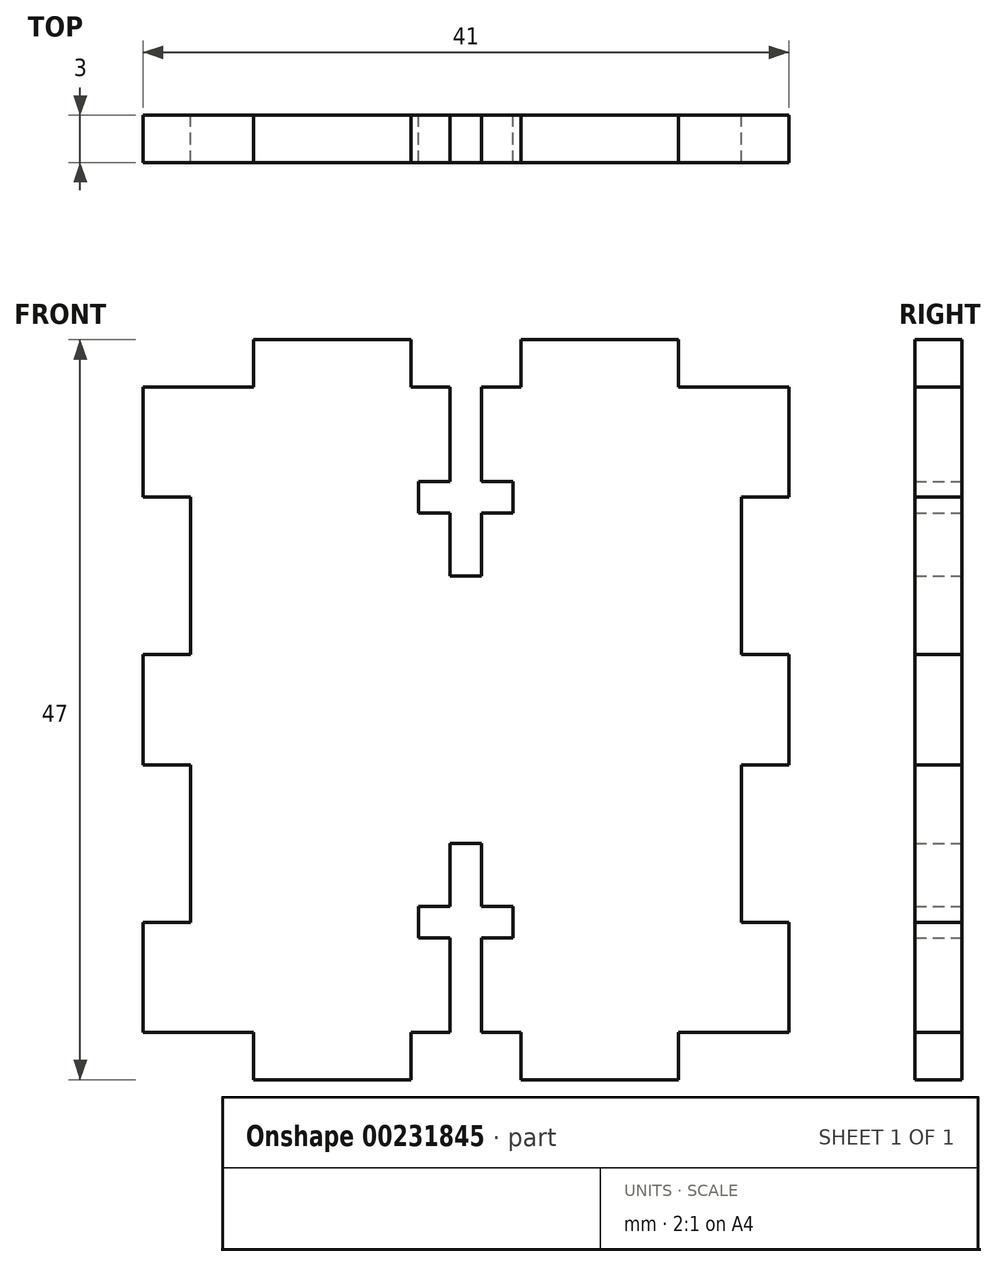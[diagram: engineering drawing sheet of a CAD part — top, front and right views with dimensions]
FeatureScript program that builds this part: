
annotation { "Feature Type Name" : "Feature", "Feature Type Description" : "" }
export const myFeature = defineFeature(function(context is Context, id is Id, definition is map)
    precondition{}
    {
        {
            var Q0;
            Q0=qCreatedBy(makeId("Front.planeOp"),FACE);
            var sketch = newSketch(context, id + "F0", { "sketchPlane" : qUnion([Q0])});
            skLineSegment(sketch, "E0", {"start": v(0, 0) * mm, "end": v(0, 3.5) * mm});
            skLineSegment(sketch, "E1", {"start": v(0, 3.5) * mm, "end": v(3, 3.5) * mm});
            skLineSegment(sketch, "E2", {"start": v(3, 3.5) * mm, "end": v(3, 13.5) * mm});
            skLineSegment(sketch, "E3", {"start": v(3, 13.5) * mm, "end": v(0, 13.5) * mm});
            skLineSegment(sketch, "E4", {"start": v(0, 13.5) * mm, "end": v(0, 20.5) * mm});
            skLineSegment(sketch, "E5", {"start": v(0, 20.5) * mm, "end": v(7, 20.5) * mm});
            skLineSegment(sketch, "E6", {"start": v(7, 20.5) * mm, "end": v(7, 23.5) * mm});
            skLineSegment(sketch, "E7", {"start": v(7, 23.5) * mm, "end": v(17, 23.5) * mm});
            skLineSegment(sketch, "E8", {"start": v(17, 23.5) * mm, "end": v(17, 20.5) * mm});
            skLineSegment(sketch, "E9", {"start": v(17, 20.5) * mm, "end": v(19.5, 20.5) * mm});
            skLineSegment(sketch, "E10", {"start": v(24, 20.5) * mm, "end": v(24, 23.5) * mm});
            skLineSegment(sketch, "E11.top", {"start": v(19.5, 8.5) * mm, "end": v(21.5, 8.5) * mm});
            skLineSegment(sketch, "E11.left", {"start": v(19.5, 20.5) * mm, "end": v(19.5, 14.5) * mm});
            skLineSegment(sketch, "E11.right", {"start": v(21.5, 20.5) * mm, "end": v(21.5, 14.5) * mm});
            skLineSegment(sketch, "E12.bottom", {"start": v(17.5, 14.5) * mm, "end": v(19.5, 14.5) * mm});
            skLineSegment(sketch, "E12.top", {"start": v(17.5, 12.5) * mm, "end": v(19.5, 12.5) * mm});
            skLineSegment(sketch, "E12.left", {"start": v(17.5, 14.5) * mm, "end": v(17.5, 12.5) * mm});
            skLineSegment(sketch, "E12.right", {"start": v(23.5, 14.5) * mm, "end": v(23.5, 12.5) * mm});
            skLineSegment(sketch, "E13.trimOffspring", {"start": v(21.5, 20.5) * mm, "end": v(24, 20.5) * mm});
            skLineSegment(sketch, "E14.trimOffspring", {"start": v(19.5, 12.5) * mm, "end": v(19.5, 8.5) * mm});
            skLineSegment(sketch, "E15.trimOffspring", {"start": v(21.5, 12.5) * mm, "end": v(21.5, 8.5) * mm});
            skPoint(sketch, "E16.trimOffspring.end.orphan", {"position": v(20.5, 0) * mm});
            skLineSegment(sketch, "E17", {"start": v(24, 23.5) * mm, "end": v(34, 23.5) * mm});
            skLineSegment(sketch, "E18", {"start": v(34, 23.5) * mm, "end": v(34, 20.5) * mm});
            skLineSegment(sketch, "E19", {"start": v(34, 20.5) * mm, "end": v(41, 20.5) * mm});
            skLineSegment(sketch, "E20", {"start": v(41, 20.5) * mm, "end": v(41, 13.5) * mm});
            skLineSegment(sketch, "E21", {"start": v(38, 13.5) * mm, "end": v(41, 13.5) * mm});
            skLineSegment(sketch, "E22", {"start": v(38, 13.5) * mm, "end": v(38, 3.5) * mm});
            skLineSegment(sketch, "E23", {"start": v(38, 3.5) * mm, "end": v(41, 3.5) * mm});
            skLineSegment(sketch, "E24", {"start": v(41, 3.5) * mm, "end": v(41, 0) * mm});
            skLineSegment(sketch, "E25", {"start": v(0, 0) * mm, "end": v(41, 0) * mm, "construction": true});
            skLineSegment(sketch, "E26.MirrorCS", {"start": v(17.5, -12.5) * mm, "end": v(19.5, -12.5) * mm});
            skLineSegment(sketch, "E27.MirrorCS", {"start": v(34, -20.5) * mm, "end": v(41, -20.5) * mm});
            skLineSegment(sketch, "E28.MirrorCS", {"start": v(38, -3.5) * mm, "end": v(41, -3.5) * mm});
            skLineSegment(sketch, "E29.MirrorCS", {"start": v(38, -13.5) * mm, "end": v(41, -13.5) * mm});
            skLineSegment(sketch, "E30.MirrorCS", {"start": v(21.5, -12.5) * mm, "end": v(21.5, -8.5) * mm});
            skLineSegment(sketch, "E31.MirrorCS", {"start": v(38, -13.5) * mm, "end": v(38, -3.5) * mm});
            skLineSegment(sketch, "E32.MirrorCS", {"start": v(34, -23.5) * mm, "end": v(34, -20.5) * mm});
            skLineSegment(sketch, "E33.MirrorCS", {"start": v(41, -20.5) * mm, "end": v(41, -13.5) * mm});
            skLineSegment(sketch, "E34.MirrorCS", {"start": v(19.5, -8.5) * mm, "end": v(21.5, -8.5) * mm});
            skLineSegment(sketch, "E35.MirrorCS", {"start": v(24, -23.5) * mm, "end": v(34, -23.5) * mm});
            skLineSegment(sketch, "E36.MirrorCS", {"start": v(21.5, -20.5) * mm, "end": v(24, -20.5) * mm});
            skLineSegment(sketch, "E37.MirrorCS", {"start": v(17.5, -14.5) * mm, "end": v(17.5, -12.5) * mm});
            skLineSegment(sketch, "E38.MirrorCS", {"start": v(19.5, -20.5) * mm, "end": v(19.5, -14.5) * mm});
            skLineSegment(sketch, "E39.MirrorCS", {"start": v(19.5, -12.5) * mm, "end": v(19.5, -8.5) * mm});
            skLineSegment(sketch, "E40.MirrorCS", {"start": v(17, -23.5) * mm, "end": v(17, -20.5) * mm});
            skLineSegment(sketch, "E41.MirrorCS", {"start": v(0, -20.5) * mm, "end": v(7, -20.5) * mm});
            skLineSegment(sketch, "E42.MirrorCS", {"start": v(17.5, -14.5) * mm, "end": v(19.5, -14.5) * mm});
            skLineSegment(sketch, "E43.MirrorCS", {"start": v(41, -3.5) * mm, "end": v(41, 0) * mm});
            skLineSegment(sketch, "E44.MirrorCS", {"start": v(0, -13.5) * mm, "end": v(0, -20.5) * mm});
            skLineSegment(sketch, "E45.MirrorCS", {"start": v(7, -23.5) * mm, "end": v(17, -23.5) * mm});
            skLineSegment(sketch, "E46.MirrorCS", {"start": v(21.5, -20.5) * mm, "end": v(21.5, -14.5) * mm});
            skLineSegment(sketch, "E47.MirrorCS", {"start": v(17, -20.5) * mm, "end": v(19.5, -20.5) * mm});
            skLineSegment(sketch, "E48.MirrorCS", {"start": v(0, -3.5) * mm, "end": v(3, -3.5) * mm});
            skLineSegment(sketch, "E49.MirrorCS", {"start": v(0, 0) * mm, "end": v(0, -3.5) * mm});
            skLineSegment(sketch, "E50.MirrorCS", {"start": v(3, -3.5) * mm, "end": v(3, -13.5) * mm});
            skLineSegment(sketch, "E51.MirrorCS", {"start": v(3, -13.5) * mm, "end": v(0, -13.5) * mm});
            skLineSegment(sketch, "E52.MirrorCS", {"start": v(24, -20.5) * mm, "end": v(24, -23.5) * mm});
            skLineSegment(sketch, "E53.MirrorCS", {"start": v(23.5, -14.5) * mm, "end": v(23.5, -12.5) * mm});
            skLineSegment(sketch, "E54.MirrorCS", {"start": v(7, -20.5) * mm, "end": v(7, -23.5) * mm});
            skLineSegment(sketch, "E55.trimOffspring", {"start": v(21.5, -12.5) * mm, "end": v(23.5, -12.5) * mm});
            skPoint(sketch, "E56.MirrorCS.end.orphan", {"position": v(20.5, -14.5) * mm});
            skPoint(sketch, "E56.MirrorCS.start.orphan", {"position": v(20.5, -20.5) * mm});
            skPoint(sketch, "E57.end.orphan", {"position": v(20.5, 14.5) * mm});
            skPoint(sketch, "E57.start.orphan", {"position": v(20.5, 20.5) * mm});
            skLineSegment(sketch, "E58.trimOffspring", {"start": v(21.5, 12.5) * mm, "end": v(23.5, 12.5) * mm});
            skLineSegment(sketch, "E59.trimOffspring", {"start": v(21.5, -14.5) * mm, "end": v(23.5, -14.5) * mm});
            skLineSegment(sketch, "E60.trimOffspring", {"start": v(21.5, 14.5) * mm, "end": v(23.5, 14.5) * mm});
            skSolve(sketch);
        }
        {
            var Q0;
            Q0=makeQuery(id+"F0.imprint","IMPRINT",FACE,{"disambiguationData":[TD([[makeQuery(id+"F0.imprint","IMPRINT",EDGE,{"derivedFrom":sQuery(id+"F0.wireOp",EDGE,"E0")}),-1.0]])]});
            extrude(context, id + "F1", {"entities" : qUnion([Q0]), "depth" : 3 * mm});
        }
    });
